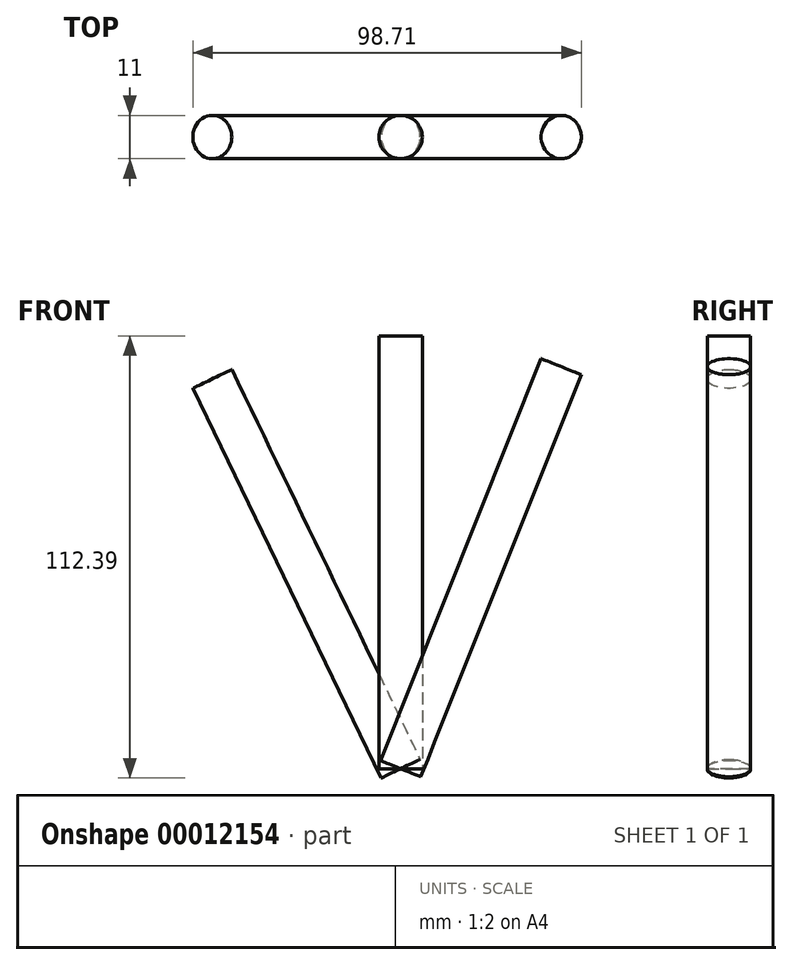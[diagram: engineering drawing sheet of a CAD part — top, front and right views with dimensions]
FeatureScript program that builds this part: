
annotation { "Feature Type Name" : "Feature", "Feature Type Description" : "" }
export const myFeature = defineFeature(function(context is Context, id is Id, definition is map)
    precondition{}
    {
        {
            var Q0;
            Q0=qCreatedBy(makeId("Right.planeOp"),FACE);
            var sketch = newSketch(context, id + "F0", { "sketchPlane" : qUnion([Q0])});
            skLineSegment(sketch, "E0", {"start": v(0, 0) * mm, "end": v(34.2, 0) * mm, "construction": true});
            skSolve(sketch);
        }
        {
            var Q0;
            Q0=qCreatedBy(makeId("Top.planeOp"),FACE);
            var sketch = newSketch(context, id + "F1", { "sketchPlane" : qUnion([Q0])});
            skCircle(sketch, "E1", {"center": v(0, 0) * mm, "radius": 5.5 * mm});
            skSolve(sketch);
        }
        {
            var Q0;
            Q0 = qSketchRegion(id + "F1", true);
            extrude(context, id + "F2", {"entities" : qUnion([Q0]), "depth" : 110 * mm});
        }
        {
            var Q0;
            Q0=makeQuery(id+"F2.opExtrude","SWEPT_BODY",BODY,{"disambiguationData":[OSD([sQuery(id+"F1.wireOp",EDGE,"E1")])]});
            var Q1;
            Q1=sQuery(id+"F0.wireOp",EDGE,"E0");
            transform(context, id + "F3", {"entities" : qUnion([Q0]), "transformType" : TransformType.ROTATION, "transformAxis" : qUnion([Q1]), "angle" : 0.45 * radian, "oppositeDirection" : true, "makeCopy" : true});
        }
        {
            var Q0;
            Q0=makeQuery(id+"F2.opExtrude","SWEPT_BODY",BODY,{"disambiguationData":[OSD([sQuery(id+"F1.wireOp",EDGE,"E1")])]});
            var Q1;
            Q1=sQuery(id+"F0.wireOp",EDGE,"E0");
            transform(context, id + "F4", {"entities" : qUnion([Q0]), "transformType" : TransformType.ROTATION, "transformAxis" : qUnion([Q1]), "angle" : 0.38 * radian, "makeCopy" : true});
        }
    });
